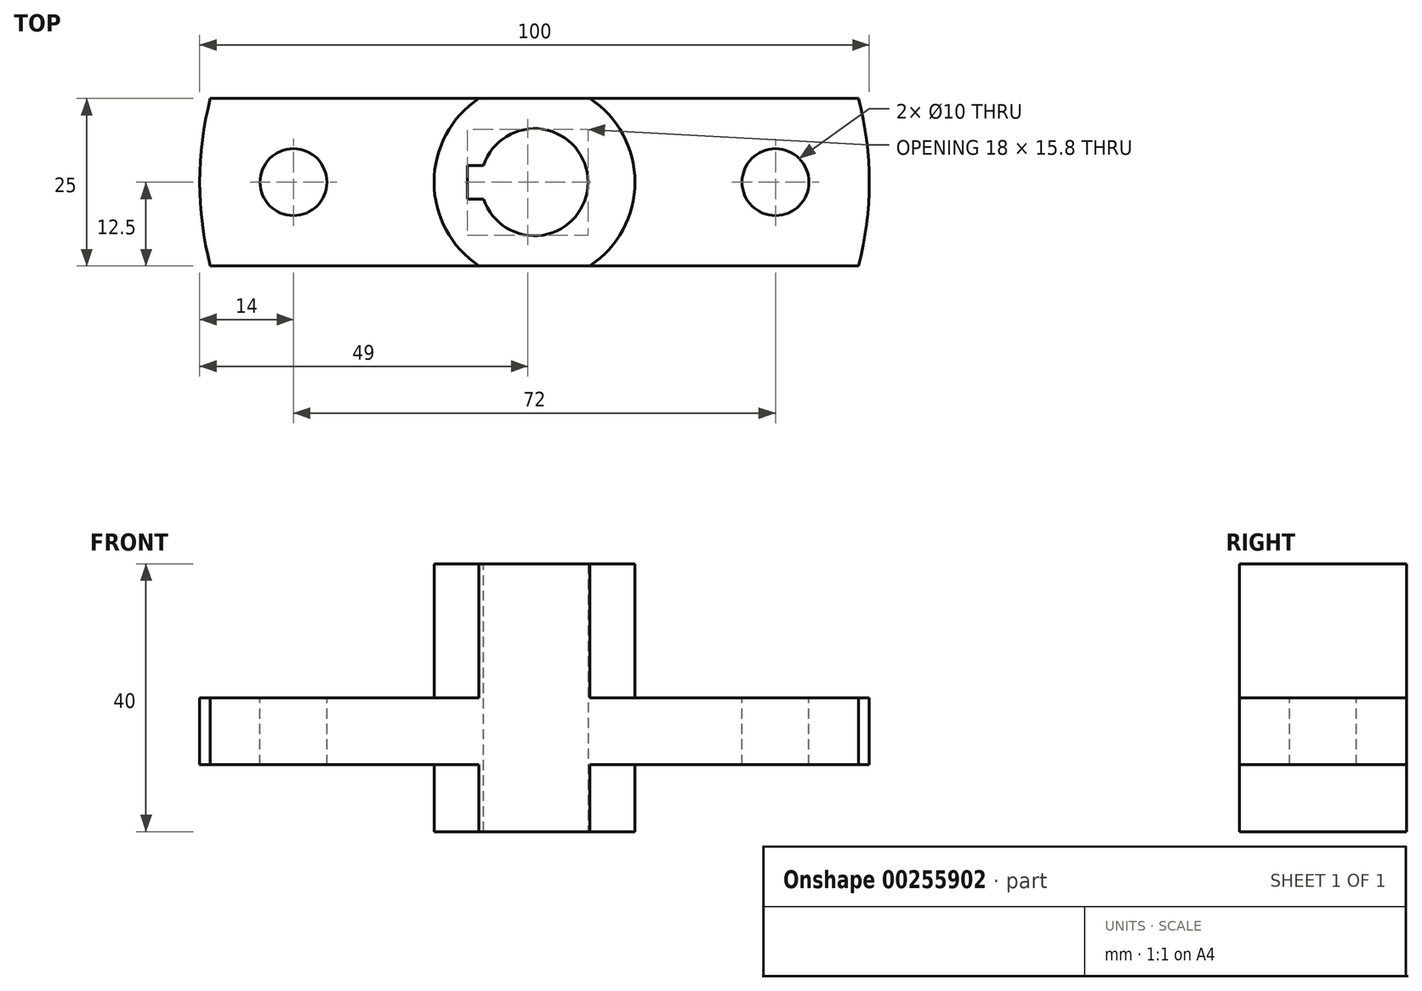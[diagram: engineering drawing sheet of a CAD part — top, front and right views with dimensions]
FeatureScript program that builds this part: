
annotation { "Feature Type Name" : "Feature", "Feature Type Description" : "" }
export const myFeature = defineFeature(function(context is Context, id is Id, definition is map)
    precondition{}
    {
        {
            var Q0;
            Q0=qCreatedBy(makeId("Top.planeOp"),FACE);
            var sketch = newSketch(context, id + "F0", { "sketchPlane" : qUnion([Q0])});
            skArc(sketch, "E0", {"start": v(0, -8) * mm, "mid": v(8, 0) * mm, "end": v(0, 8) * mm});
            skArc(sketch, "E1", {"start": v(8.3, -12.5) * mm, "mid": v(15, 0) * mm, "end": v(8.3, 12.5) * mm});
            skArc(sketch, "E2", {"start": v(48.41, -12.5) * mm, "mid": v(50, 0) * mm, "end": v(48.41, 12.5) * mm});
            skLineSegment(sketch, "E3", {"start": v(0, 12.5) * mm, "end": v(0, 8) * mm});
            skLineSegment(sketch, "E4", {"start": v(0, 12.5) * mm, "end": v(48.41, 12.5) * mm});
            skLineSegment(sketch, "E5", {"start": v(0, -12.5) * mm, "end": v(48.41, -12.5) * mm});
            skPoint(sketch, "E6.orphan", {"position": v(0, 50) * mm});
            skLineSegment(sketch, "E7.trimOffspring", {"start": v(0, -15) * mm, "end": v(0, -50) * mm});
            skCircle(sketch, "E8", {"center": v(36, 0) * mm, "radius": 5 * mm});
            skLineSegment(sketch, "E9.trimOffspring", {"start": v(0, -8) * mm, "end": v(0, -12.5) * mm});
            skSolve(sketch);
        }
        {
            var Q0;
            Q0=makeQuery(id+"F0.imprint","IMPRINT",FACE,{"disambiguationData":[TD([[makeQuery(id+"F0.imprint","IMPRINT",EDGE,{"derivedFrom":sQuery(id+"F0.wireOp",EDGE,"E0")}),-1.0]])]});
            extrude(context, id + "F1", {"entities" : qUnion([Q0]), "endBound" : BoundingType.SYMMETRIC, "depth" : 40 * mm});
        }
        {
            var Q0;
            {var subQ1=sQuery(id+"F0.wireOp",EDGE,"E1");Q0=makeQuery(id+"F0.imprint","IMPRINT",FACE,{"disambiguationData":[TD([[makeQuery(id+"F0.imprint","IMPRINT",EDGE,{"derivedFrom":subQ1}),-1.0]])]});}
            extrude(context, id + "F2", {"entities" : qUnion([Q0]), "operationType" : NewBodyOperationType.ADD, "oppositeDirection" : true, "depth" : 10 * mm});
        }
        {
            var Q0;
            Q0=makeQuery(id+"F1.opExtrude","SWEPT_BODY",BODY,{"disambiguationData":[OSD([sQuery(id+"F0.wireOp",EDGE,"E0"),sQuery(id+"F0.wireOp",EDGE,"E1"),sQuery(id+"F0.wireOp",EDGE,"E3"),sQuery(id+"F0.wireOp",EDGE,"E4"),sQuery(id+"F0.wireOp",EDGE,"E5"),sQuery(id+"F0.wireOp",EDGE,"E9.trimOffspring")])]});
            var Q1;
            Q1=qCreatedBy(makeId("Right.planeOp"),FACE);
            mirror(context, id + "F3", {"operationType" : NewBodyOperationType.ADD, "entities" : qUnion([Q0]), "mirrorPlane" : qUnion([Q1])});
        }
        {
            var Q0;
            {var subQ0=makeQuery(id+"F1.opExtrude","CAP_FACE",FACE,{"disambiguationData":[OSD([sQuery(id+"F0.wireOp",EDGE,"E0"),sQuery(id+"F0.wireOp",EDGE,"E1"),sQuery(id+"F0.wireOp",EDGE,"E3"),sQuery(id+"F0.wireOp",EDGE,"E4"),sQuery(id+"F0.wireOp",EDGE,"E5"),sQuery(id+"F0.wireOp",EDGE,"E9.trimOffspring")])],"isStart":false});Q0=makeQuery(id+"F3.boolean.opBoolean","MERGE",FACE,{"derivedFrom":[subQ0,makeQuery(id+"F3.opPattern","COPY",FACE,{"derivedFrom":subQ0,"instanceName":"1"})]});}
            var sketch = newSketch(context, id + "F4", { "sketchPlane" : qUnion([Q0])});
            skLineSegment(sketch, "E10.bottom", {"start": v(-10, 2.5) * mm, "end": v(-1.45, 2.5) * mm});
            skLineSegment(sketch, "E10.top", {"start": v(-10, -2.5) * mm, "end": v(-1.45, -2.5) * mm});
            skLineSegment(sketch, "E10.left", {"start": v(-10, 2.5) * mm, "end": v(-10, -2.5) * mm});
            skLineSegment(sketch, "E10.right", {"start": v(-1.45, 2.5) * mm, "end": v(-1.45, -2.5) * mm});
            skPoint(sketch, "E10.middle", {"position": v(-5.72, 0) * mm});
            skSolve(sketch);
        }
        {
            var Q0;
            {var subQ0=sQuery(id+"F4.wireOp",EDGE,"E10.left");Q0=makeQuery(id+"F4.imprint","IMPRINT",FACE,{"disambiguationData":[TD([[makeQuery(id+"F4.imprint","IMPRINT",EDGE,{"derivedFrom":subQ0}),1.0]])]});}
            extrude(context, id + "F5", {"entities" : qUnion([Q0]), "operationType" : NewBodyOperationType.REMOVE, "endBound" : BoundingType.THROUGH_ALL, "oppositeDirection" : true, "depth" : 25 * mm});
        }
    });
